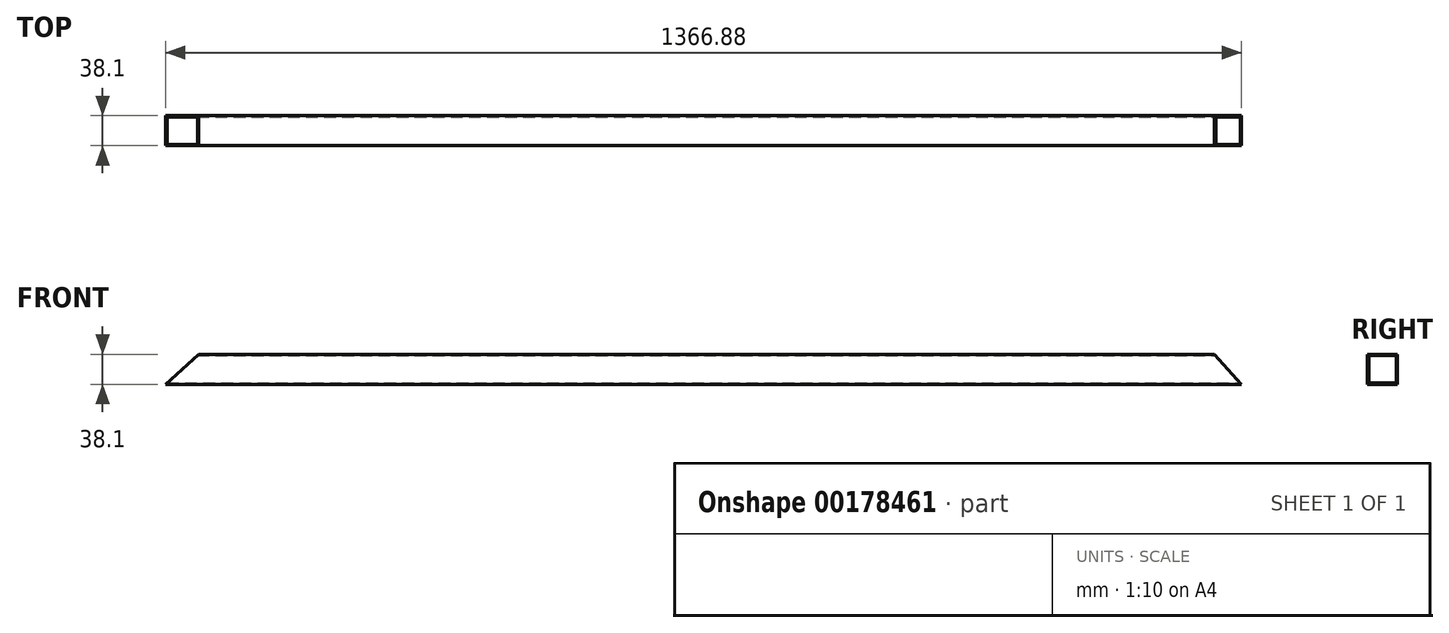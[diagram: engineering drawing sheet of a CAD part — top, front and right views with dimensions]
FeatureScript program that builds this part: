
annotation { "Feature Type Name" : "Feature", "Feature Type Description" : "" }
export const myFeature = defineFeature(function(context is Context, id is Id, definition is map)
    precondition{}
    {
        {
            var Q0;
            Q0=qCreatedBy(makeId("Front.planeOp"),FACE);
            var sketch = newSketch(context, id + "F0", { "sketchPlane" : qUnion([Q0])});
            skLineSegment(sketch, "E0", {"start": v(683.44, 0) * mm, "end": v(683.44, -38.1) * mm});
            skLineSegment(sketch, "E1", {"start": v(-683.44, 0) * mm, "end": v(-683.44, -38.1) * mm});
            skLineSegment(sketch, "E2", {"start": v(-683.44, -38.1) * mm, "end": v(683.44, -38.1) * mm});
            skLineSegment(sketch, "E3", {"start": v(-683.44, 0) * mm, "end": v(683.44, 0) * mm});
            skSolve(sketch);
        }
        {
            var Q0;
            Q0=makeQuery(id+"F0.imprint","IMPRINT",FACE,{"disambiguationData":[TD([[makeQuery(id+"F0.imprint","IMPRINT",EDGE,{"derivedFrom":sQuery(id+"F0.wireOp",EDGE,"HqZMai2i-7OOq-6NAL-NtFz-gxplS83oMwde")}),1.0]])]});
            var Q1;
            Q1=makeQuery(id+"F0.imprint","IMPRINT",FACE,{"disambiguationData":[TD([[makeQuery(id+"F0.imprint","IMPRINT",EDGE,{"derivedFrom":sQuery(id+"F0.wireOp",EDGE,"E0")}),-1.0]])]});
            extrude(context, id + "F1", {"entities" : qUnion([Q0, Q1]), "depth" : 38.1 * mm});
        }
        {
            var Q0;
            Q0=qCreatedBy(makeId("Right.planeOp"),FACE);
            var sketch = newSketch(context, id + "F2", { "sketchPlane" : qUnion([Q0])});
            skLineSegment(sketch, "E4.bottom", {"start": v(-36.45, -1.65) * mm, "end": v(-1.65, -1.65) * mm});
            skLineSegment(sketch, "E4.top", {"start": v(-36.45, -36.45) * mm, "end": v(-1.65, -36.45) * mm});
            skLineSegment(sketch, "E4.left", {"start": v(-36.45, -1.65) * mm, "end": v(-36.45, -36.45) * mm});
            skLineSegment(sketch, "E4.right", {"start": v(-1.65, -1.65) * mm, "end": v(-1.65, -36.45) * mm});
            skPoint(sketch, "E4.middle", {"position": v(-19.05, -19.05) * mm});
            skSolve(sketch);
        }
        {
            var Q0;
            Q0 = qSketchRegion(id + "F2", true);
            extrude(context, id + "F3", {"entities" : qUnion([Q0]), "operationType" : NewBodyOperationType.REMOVE, "endBound" : BoundingType.THROUGH_ALL, "oppositeDirection" : true, "depth" : 25.4 * mm, "hasSecondDirection" : true, "secondDirectionBound" : SecondDirectionBoundingType.THROUGH_ALL, "secondDirectionOppositeDirection" : false, "secondDirectionDepth" : 25.4 * mm});
        }
        {
            var Q0;
            Q0=makeQuery(id+"F1.opExtrude","CAP_FACE",FACE,{"disambiguationData":[OSD([sQuery(id+"F0.wireOp",EDGE,"E0"),sQuery(id+"F0.wireOp",EDGE,"E1"),sQuery(id+"F0.wireOp",EDGE,"E2"),sQuery(id+"F0.wireOp",EDGE,"E3")])],"isStart":false});
            var sketch = newSketch(context, id + "F4", { "sketchPlane" : qUnion([Q0])});
            skLineSegment(sketch, "E5", {"start": v(-683.44, -38.1) * mm, "end": v(-641.11, 0) * mm});
            skLineSegment(sketch, "E6", {"start": v(-641.11, 0) * mm, "end": v(-683.44, 0) * mm});
            skLineSegment(sketch, "E7", {"start": v(-683.44, 0) * mm, "end": v(-683.44, -38.1) * mm});
            skLineSegment(sketch, "E8", {"start": v(683.44, -38.1) * mm, "end": v(649.15, 0) * mm});
            skLineSegment(sketch, "E9", {"start": v(649.15, 0) * mm, "end": v(683.44, 0) * mm});
            skLineSegment(sketch, "E10", {"start": v(683.44, 0) * mm, "end": v(683.44, -38.1) * mm});
            skSolve(sketch);
        }
        {
            var Q0;
            Q0=makeQuery(id+"F4.imprint","IMPRINT",FACE,{"disambiguationData":[TD([[makeQuery(id+"F4.imprint","IMPRINT",EDGE,{"derivedFrom":sQuery(id+"F4.wireOp",EDGE,"E8")}),-1.0]])]});
            var Q1;
            Q1=makeQuery(id+"F4.imprint","IMPRINT",FACE,{"disambiguationData":[TD([[makeQuery(id+"F4.imprint","IMPRINT",EDGE,{"derivedFrom":sQuery(id+"F4.wireOp",EDGE,"E5")}),1.0]])]});
            extrude(context, id + "F5", {"entities" : qUnion([Q0, Q1]), "operationType" : NewBodyOperationType.REMOVE, "endBound" : BoundingType.THROUGH_ALL, "oppositeDirection" : true, "depth" : 25.4 * mm});
        }
    });
